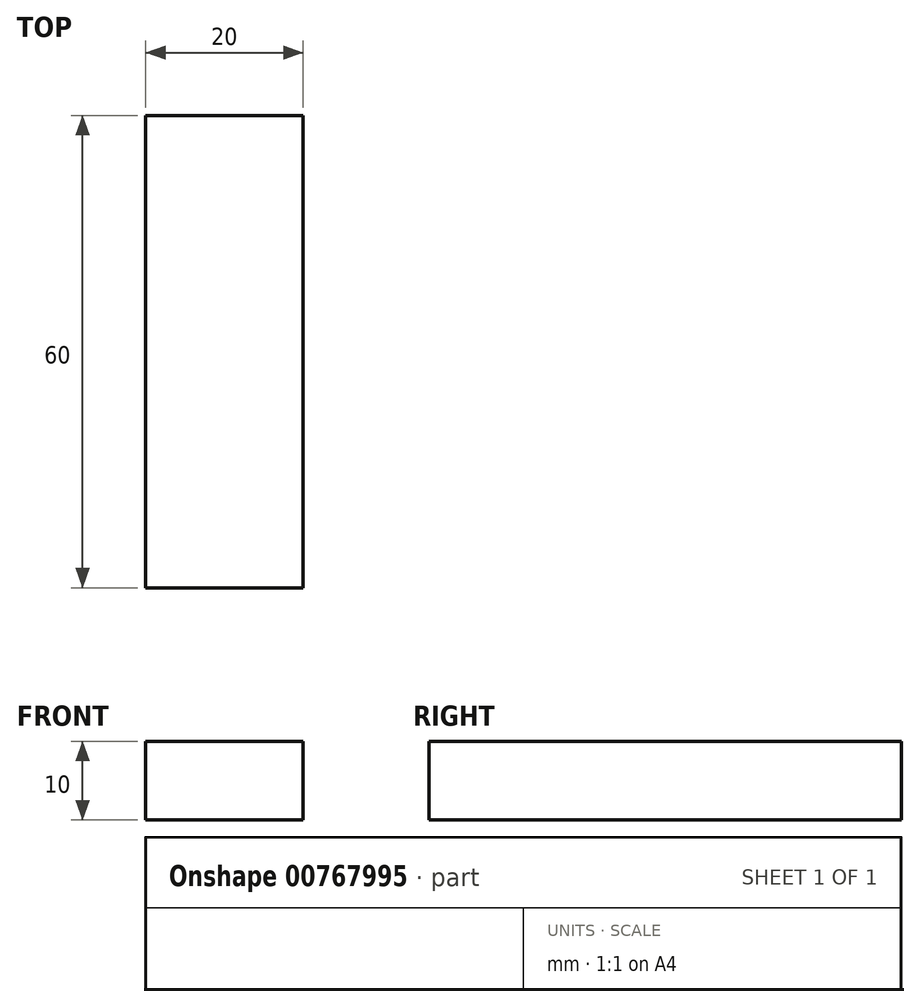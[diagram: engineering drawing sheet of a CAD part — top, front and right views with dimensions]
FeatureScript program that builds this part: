
annotation { "Feature Type Name" : "Feature", "Feature Type Description" : "" }
export const myFeature = defineFeature(function(context is Context, id is Id, definition is map)
    precondition{}
    {
        {
            var Q0;
            Q0=qCreatedBy(makeId("Top.planeOp"),FACE);
            var sketch = newSketch(context, id + "F0", { "sketchPlane" : qUnion([Q0])});
            skLineSegment(sketch, "E0.bottom", {"start": v(-40.15, 36.4) * mm, "end": v(-20.15, 36.4) * mm});
            skLineSegment(sketch, "E0.top", {"start": v(-40.15, -23.6) * mm, "end": v(-20.15, -23.6) * mm});
            skLineSegment(sketch, "E0.left", {"start": v(-40.15, 36.4) * mm, "end": v(-40.15, -23.6) * mm});
            skLineSegment(sketch, "E0.right", {"start": v(-20.15, 36.4) * mm, "end": v(-20.15, -23.6) * mm});
            skSolve(sketch);
        }
        {
            var Q0;
            Q0=makeQuery(id+"F0.imprint","IMPRINT",FACE,{"disambiguationData":[TD([[makeQuery(id+"F0.imprint","IMPRINT",EDGE,{"derivedFrom":sQuery(id+"F0.wireOp",EDGE,"E0.bottom")}),-1.0]])]});
            extrude(context, id + "F1", {"entities" : qUnion([Q0]), "depth" : 10 * mm, "offsetDistance" : 25 * mm});
        }
    });
